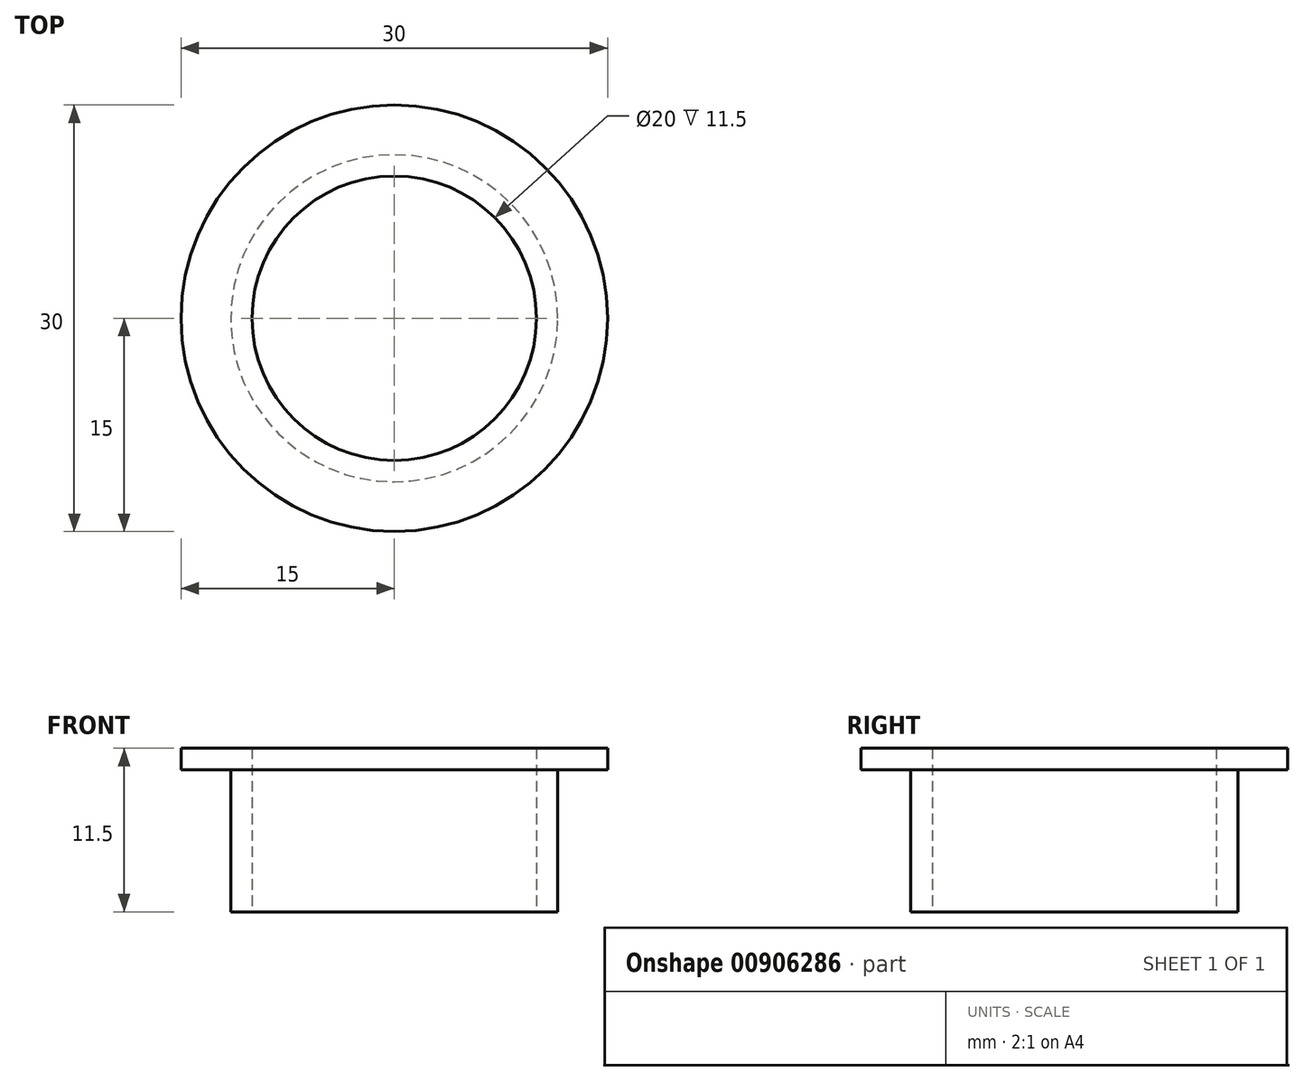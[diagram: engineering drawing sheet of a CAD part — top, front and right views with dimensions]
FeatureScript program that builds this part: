
annotation { "Feature Type Name" : "Feature", "Feature Type Description" : "" }
export const myFeature = defineFeature(function(context is Context, id is Id, definition is map)
    precondition{}
    {
        {
            var Q0;
            Q0=qCreatedBy(makeId("Front.planeOp"),FACE);
            var sketch = newSketch(context, id + "F0", { "sketchPlane" : qUnion([Q0])});
            skLineSegment(sketch, "E0", {"start": v(-10, 0) * mm, "end": v(-10, 11.5) * mm});
            skLineSegment(sketch, "E1", {"start": v(-10, 11.5) * mm, "end": v(-15, 11.5) * mm});
            skLineSegment(sketch, "E2", {"start": v(-15, 11.5) * mm, "end": v(-15, 10) * mm});
            skLineSegment(sketch, "E3", {"start": v(-15, 10) * mm, "end": v(-11.5, 10) * mm});
            skLineSegment(sketch, "E4", {"start": v(-11.5, 10) * mm, "end": v(-11.5, 0) * mm});
            skLineSegment(sketch, "E5", {"start": v(-11.5, 0) * mm, "end": v(-10, 0) * mm});
            skLineSegment(sketch, "E6", {"start": v(0, 0) * mm, "end": v(0, 20.28) * mm});
            skSolve(sketch);
        }
        {
            var Q0;
            Q0=makeQuery(id+"F0.imprint","IMPRINT",FACE,{"disambiguationData":[TD([[makeQuery(id+"F0.imprint","IMPRINT",EDGE,{"derivedFrom":sQuery(id+"F0.wireOp",EDGE,"E0")}),1.0]])]});
            var Q1;
            Q1=sQuery(id+"F0.wireOp",EDGE,"E6");
            revolve(context, id + "F1", {"surfaceOperationType" : NewSurfaceOperationType.NEW, "entities" : qUnion([Q0]), "axis" : qUnion([Q1]), "revolveType" : RevolveType.FULL});
        }
    });
